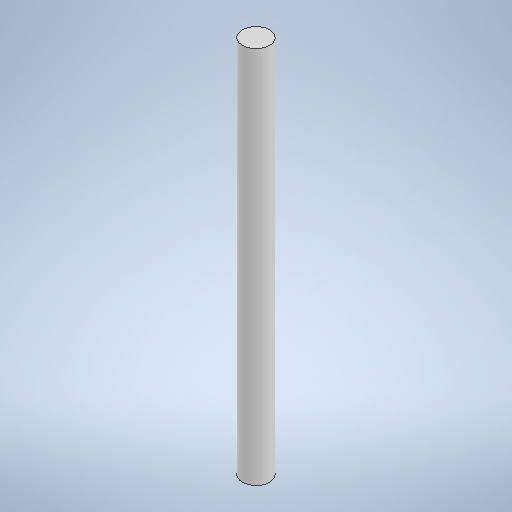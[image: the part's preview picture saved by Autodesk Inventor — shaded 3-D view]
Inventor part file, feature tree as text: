
AUTODESK INVENTOR PART (.ipt)
format: ipt  version: 2025 (Build 290162000, 162)  size: 247,296 bytes
history: native  units: mm
features: other x1, extrude x1, sketch x1
ambient origin geometry x8: Origin, YZ Plane, XZ Plane, XY Plane, X Axis, Y Axis, Z Axis, Center Point
bodies: Body1 (feature_tree)
feature tree (3):
  other  "Bryła1"
  extrude  "Wyciągnięcie proste1"  Depth=8.0mm
  sketch  "Szkic1"
